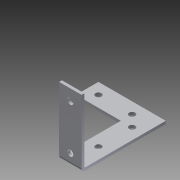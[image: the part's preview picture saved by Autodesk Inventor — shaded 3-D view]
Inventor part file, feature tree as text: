
AUTODESK INVENTOR PART (.ipt)
format: ipt  version: 2014 SP1 (Build 180222100, 222)  size: 129,024 bytes
history: native  units: in
note: dims shown in document units (in); Inventor stores cm internally (conversion verified against a paired STEP export)
features: sheet_metal_op x3, sketch x3, other x3
ambient origin geometry x8: Origin, YZ Plane, XZ Plane, XY Plane, X Axis, Y Axis, Z Axis, Center Point
bodies: Solid1 (feature_tree)
feature tree (9):
  sheet_metal_op  "Face1"
  sheet_metal_op  "Flange1"
  sketch  "Sketch1"  dims[d0=3.0in d1=1.0in d2=2.0in d3=2.0in d4=1.0in d5=0.266in d6=0.266in d7=0.266in d8=0.266in d9=0.5in d10=0.0in d11=0.5in d12=0.5in d13=0.5in d15=0.5in]
  other  "Plate1"
  sketch  "Sketch2"  dims[d17=0.75in]
  other  "Plate2"
  sheet_metal_op  "Bend1"
  sketch  "Sketch3"  dims[d18=0.125in d19=0.125in d20=0.0625in d21=0.25in d22=0.125in d23=3.0in d24=90.0deg d25=0.05in d26=0.5in d27=0.125in d28=0.125in d29=0.266in d30=0.266in d31=0.5in d32=2.0in d33=0.125in d34=0.0in]
  other  "Cut1"
